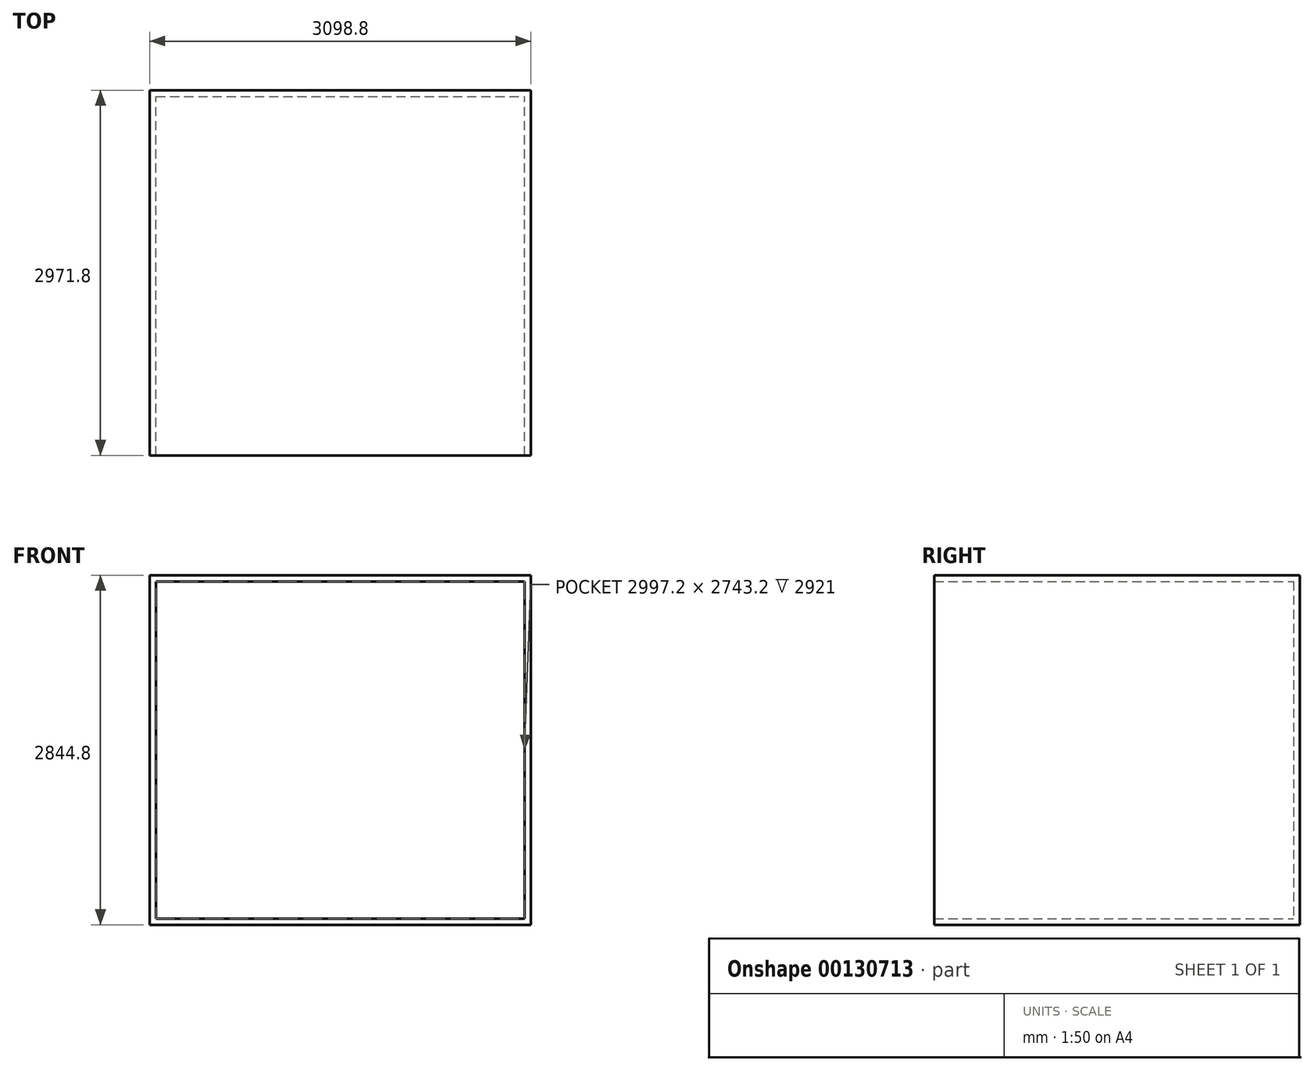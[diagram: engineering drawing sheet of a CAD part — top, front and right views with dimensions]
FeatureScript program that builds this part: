
annotation { "Feature Type Name" : "Feature", "Feature Type Description" : "" }
export const myFeature = defineFeature(function(context is Context, id is Id, definition is map)
    precondition{}
    {
        {
            var Q0;
            Q0=qCreatedBy(makeId("Top.planeOp"),FACE);
            var sketch = newSketch(context, id + "F0", { "sketchPlane" : qUnion([Q0])});
            skLineSegment(sketch, "E0.bottom", {"start": v(0, 32.98) * mm, "end": v(2997.2, 32.98) * mm});
            skLineSegment(sketch, "E0.top", {"start": v(0, 2953.98) * mm, "end": v(2997.2, 2953.98) * mm});
            skLineSegment(sketch, "E0.left", {"start": v(0, 32.98) * mm, "end": v(0, 2953.98) * mm});
            skLineSegment(sketch, "E0.right", {"start": v(2997.2, 32.98) * mm, "end": v(2997.2, 2953.98) * mm});
            skSolve(sketch);
        }
        {
            var Q0;
            Q0 = qSketchRegion(id + "F0", true);
            extrude(context, id + "F1", {"entities" : qUnion([Q0]), "depth" : 2743.2 * mm});
        }
        {
            var Q0;
            Q0=makeQuery(id+"F1.opExtrude","SWEPT_FACE",FACE,{"disambiguationData":[OSD([sQuery(id+"F0.wireOp",EDGE,"E0.bottom")])]});
            shell(context, id + "F2", {"entities" : qUnion([Q0]), "thickness" : 50.8 * mm, "oppositeDirection" : true});
        }
    });
